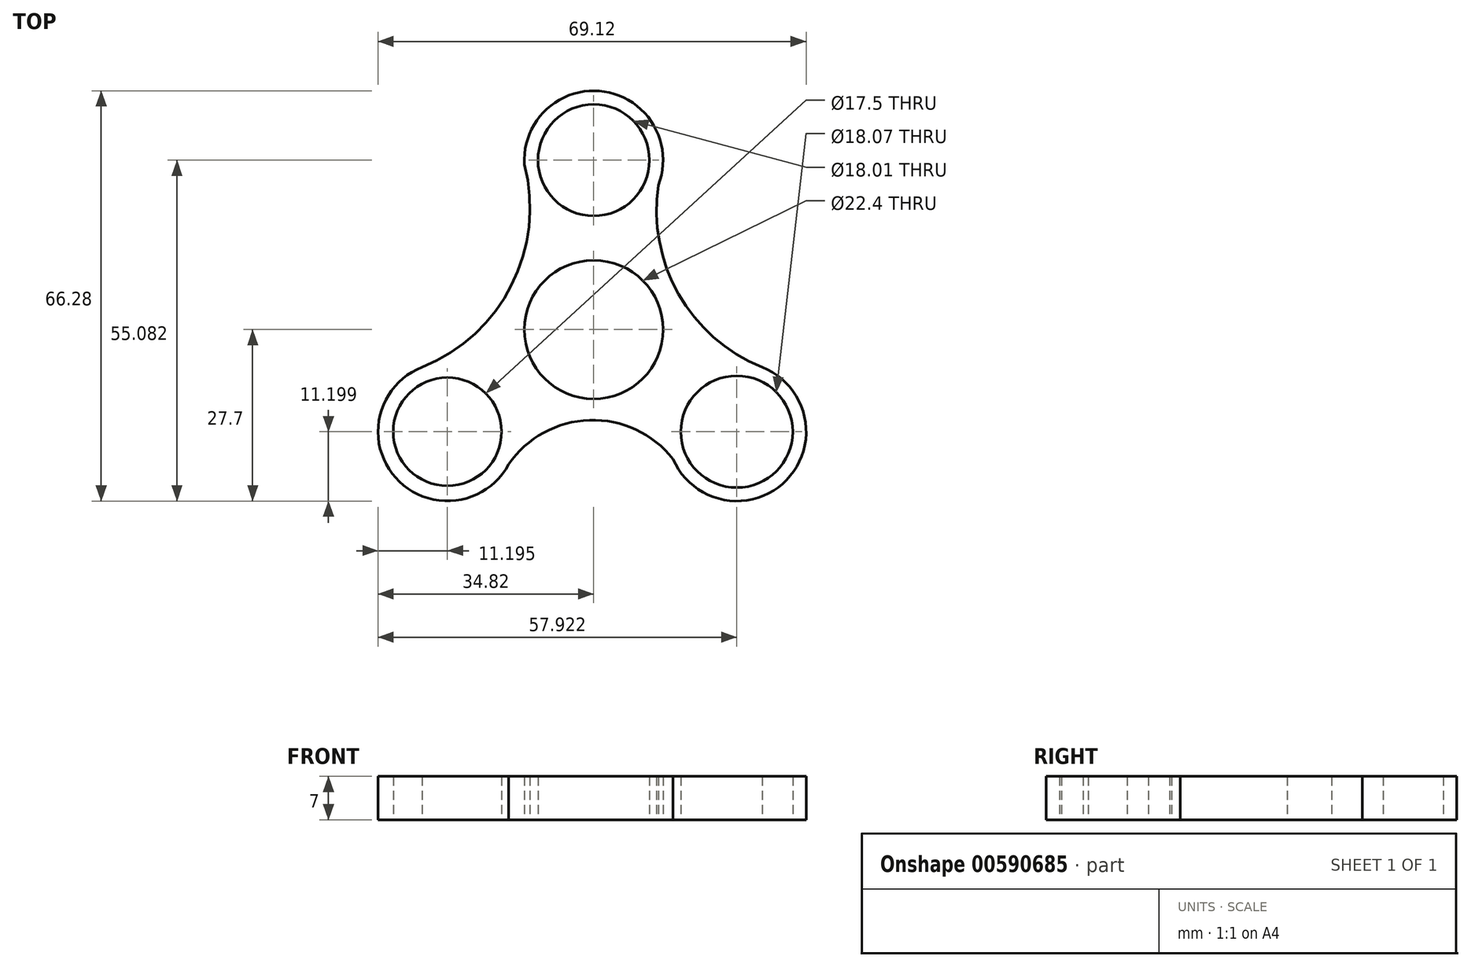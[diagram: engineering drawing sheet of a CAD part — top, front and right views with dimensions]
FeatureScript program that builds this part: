
annotation { "Feature Type Name" : "Feature", "Feature Type Description" : "" }
export const myFeature = defineFeature(function(context is Context, id is Id, definition is map)
    precondition{}
    {
        {
            var Q0;
            Q0=qCreatedBy(makeId("Top.planeOp"),FACE);
            var sketch = newSketch(context, id + "F0", { "sketchPlane" : qUnion([Q0])});
            skCircle(sketch, "E0", {"center": v(0, 0) * mm, "radius": 11.2 * mm});
            skArc(sketch, "E1", {"start": v(10.45, 23.35) * mm, "mid": v(0.18, 38.58) * mm, "end": v(-10.58, 23.7) * mm});
            skArc(sketch, "E2.2.0", {"start": v(-27.7, -6.07) * mm, "mid": v(-32, -23.94) * mm, "end": v(-13.75, -21.78) * mm});
            skPoint(sketch, "E2.center", {"position": v(-0.4, -0.7) * mm});
            skLineSegment(sketch, "E2.anchor1", {"start": v(-0.4, -0.7) * mm, "end": v(0, 27.38) * mm, "construction": true});
            skLineSegment(sketch, "E2.anchor2", {"start": v(-0.4, -0.7) * mm, "end": v(-23.62, -16.5) * mm, "construction": true});
            skArc(sketch, "E3", {"start": v(12.81, -20.92) * mm, "mid": v(31.15, -24.29) * mm, "end": v(27.18, -6.07) * mm});
            skArc(sketch, "E4", {"start": v(-27.7, -6.07) * mm, "mid": v(-13.27, 7.2) * mm, "end": v(-11.18, 26.7) * mm});
            skArc(sketch, "E5", {"start": v(11.18, 26.7) * mm, "mid": v(12.9, 7.25) * mm, "end": v(27.18, -6.07) * mm});
            skArc(sketch, "E6", {"start": v(12.81, -20.92) * mm, "mid": v(-0.68, -14.63) * mm, "end": v(-13.75, -21.78) * mm});
            skCircle(sketch, "E7", {"center": v(-23.62, -16.5) * mm, "radius": 8.75 * mm});
            skCircle(sketch, "E8", {"center": v(23.1, -16.5) * mm, "radius": 9.03 * mm});
            skCircle(sketch, "E9", {"center": v(0, 27.38) * mm, "radius": 9 * mm});
            skSolve(sketch);
        }
        {
            var Q0;
            {var subQ0=sQuery(id+"F0.wireOp",EDGE,"E5");var subQ1=sQuery(id+"F0.wireOp",EDGE,"E1");var subQ2=makeQuery(id+"F0.imprint","INTERSECT",VERTEX,{"disambiguationData":[OD(0.0)],"derivedFrom":[subQ1,subQ0]});Q0=makeQuery(id+"F0.imprint","IMPRINT",FACE,{"disambiguationData":[TD([[makeQuery(id+"F0.imprint","IMPRINT",EDGE,{"disambiguationData":[TD([[subQ2,-1.0]])],"derivedFrom":subQ1}),1.0]])]});}
            var Q1;
            {var subQ0=sQuery(id+"F0.wireOp",EDGE,"E4");var subQ1=sQuery(id+"F0.wireOp",EDGE,"E1");var subQ2=makeQuery(id+"F0.imprint","INTERSECT",VERTEX,{"disambiguationData":[OD(0.0)],"derivedFrom":[subQ1,subQ0]});Q1=makeQuery(id+"F0.imprint","IMPRINT",FACE,{"disambiguationData":[TD([[makeQuery(id+"F0.imprint","IMPRINT",EDGE,{"disambiguationData":[TD([[subQ2,1.0]])],"derivedFrom":subQ1}),1.0]])]});}
            var Q2;
            Q2=makeQuery(id+"F0.imprint","IMPRINT",FACE,{"disambiguationData":[TD([[makeQuery(id+"F0.imprint","IMPRINT",EDGE,{"derivedFrom":sQuery(id+"F0.wireOp",EDGE,"E0")}),-1.0]])]});
            extrude(context, id + "F1", {"entities" : qUnion([Q0, Q1, Q2]), "depth" : 7 * mm, "offsetDistance" : 25 * mm});
        }
    });
